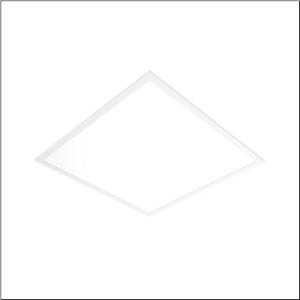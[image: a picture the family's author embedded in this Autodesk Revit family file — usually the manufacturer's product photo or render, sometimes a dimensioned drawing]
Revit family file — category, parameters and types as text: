
# Revit family: apollon_r__41_51mh12w72443_3f91
name_source: partatom
category: Lighting Fixtures
units: mm (PartAtom-declared; Revit-internal decimal feet)

## family parameters
Cut with Voids When Loaded = No
Host = Face
Light Source = No
Part Type = Normal
Room Calculation Point = No
Round Connector Dimension = Use Diameter
Shared = No

## types (1)
- Apollon® 41 (1 x LED, 3700 lm, 28.5 W, 4000K)
    Apparent Load = 29 VA
    CIE Flux Codes = 61 87 97 100 100
    Color Rendering = 80
    Color Temperature = 4000K
    Default Elevation = 1800 mm
    Description = Apollon® 41, office luminaire, primary optical cover: prismatic diffuser, of PS, light emission: direct distribution, primary light characteristic: symmetric, installation type: lay-in mounting, LED, rated luminous flux: 3.700lm, luminous efficacy: 130lm/W, light colour: 840, colour temperature: 4000K, with terminal, 3-pole, mains connection: 220..240V, AC, 50/60Hz, housing, of aluminium section, traffic white (RAL 9016), module: M600, length: 600mm, width: 600mm, height: 28mm, housing upper side, of sheet steel, protection rating (complete): IP20, protection rating (lamp compartment, on room side): IP40, insulation class (complete): insulation class II (safety insulation), certification: CE, ENEC, permissible operating ambient temperature: -25..+40°C, packaging unit: 1 piece
    Height = 0 mm  [stored 0 ft]
    Lamp = 1 x LED
    Lamp Light Flux = 3700 lm
    Lamp Power = 28.5 W
    Lamp count = 1
    Length = 600 mm
    Luminous efficacy = 130 lm/W
    Manufacturer = Siteco
    ModVariant = No
    Model = 51MH12W72443
    Mounting Place = Ceiling
    Mounting Type = Recessed
    Number of Poles = 1
    OnlyDefault = Yes
    Power Factor = 1
    Product Name = Apollon® 41
    Product group = office luminaire | ceiling recessed
    ProductGroupID = 401
    Protection Class = Protection class II
    Protection Degree = IP 20
    RLX_Detail_Level = 1
    RLX_Emergency_Light_Flux = 0 lm
    RLX_Emergency_Type = 0
    RLX_Emergency_Type_DB = No
    RlxData = <blob elided: 12189 chars, md5=c639cbf0>
    Socket = socket
    Standby Power = 0 W
    System Light Flux = 3700 lm
    System Power = 29 W
    Type Comments = Product without accessories
    Type Image = l_1291024.jpg
    URL = http://relux.com
    VarID = ---
    Voltage = 0 V
    Weight = 0.00 kg
    Width = 600 mm

note: [stored X ft] marks values corroborated as IEEE doubles in the binary element streams (Revit-internal decimal feet)

## geometry (parser evidence)
native form markers: Sweep x11
no freeform markers — native parametric forms only
